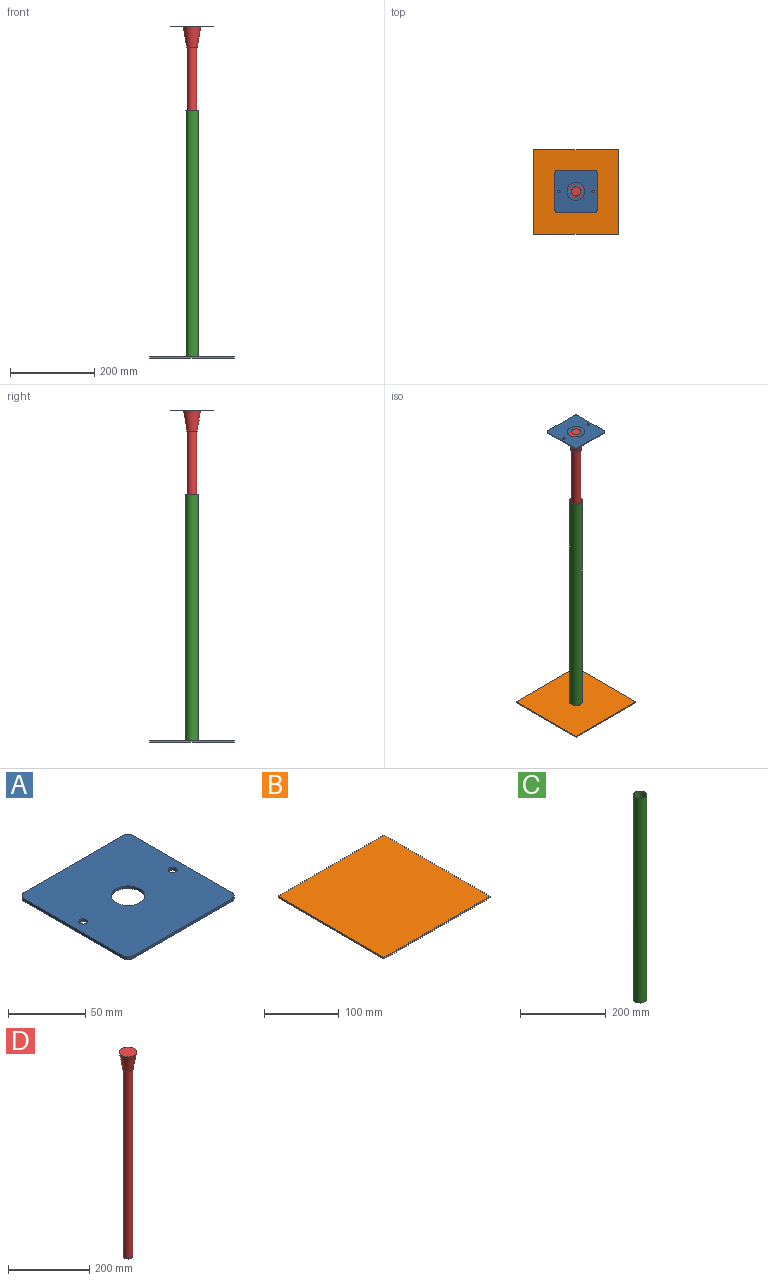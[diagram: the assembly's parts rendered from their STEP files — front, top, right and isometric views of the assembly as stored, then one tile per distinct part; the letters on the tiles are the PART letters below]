
ASSEMBLY  parts=4 mates=3
PART A: 13 faces, bbox 99.9x99.9x2.1 mm
  f0: plane 89.79x2.13mm, normal (0,-1,0), area 191.6mm2, adj f1,f7,f8,f9
  f1: cylinder r=5.08mm len=5.08mm, axis (0,0,-1), area 17mm2, adj f0,f2,f8,f9
  f2: plane 89.79x2.13mm, normal (1,0,0), area 191.6mm2, adj f1,f3,f8,f9
  f3: cylinder r=5.08mm len=5.08mm, axis (0,0,-1), area 17mm2, adj f2,f4,f8,f9
  f4: plane 89.79x2.13mm, normal (0,1,0), area 191.6mm2, adj f3,f5,f8,f9
  f5: cylinder r=5.08mm len=5.08mm, axis (0,0,-1), area 17mm2, adj f4,f6,f8,f9
  f6: plane 89.79x2.13mm, normal (-1,0,0), area 191.6mm2, adj f5,f7,f8,f9
  f7: cylinder r=5.08mm len=5.08mm, axis (0,0,-1), area 17mm2, adj f0,f6,f8,f9
  f8: plane 99.95x99.95mm, normal (0,0,1), area 9539.3mm2, adj f0,f1,f2,f3,f4,f5,f6,f7
  f9: plane 99.95x99.95mm, normal (0,0,-1), area 9539.3mm2, adj f0,f1,f2,f3,f4,f5,f6,f7
  f10: cylinder r=2.92mm len=5.84mm, axis (0,0,1), area 39.2mm2, adj f8,f9
  f11: cylinder r=2.92mm len=5.84mm, axis (0,0,1), area 39.2mm2, adj f8,f9
  f12: cylinder r=10.92mm len=21.84mm, axis (0,0,1), area 146.4mm2, adj f8,f9
PART B: 6 faces, bbox 200x200x2.5 mm
  f0: plane 200.03x2.54mm, normal (1,0,0), area 508.1mm2, adj f1,f3,f4,f5
  f1: plane 200.03x2.54mm, normal (0,1,0), area 508.1mm2, adj f0,f2,f4,f5
  f2: plane 200.03x2.54mm, normal (-1,0,0), area 508.1mm2, adj f1,f3,f4,f5
  f3: plane 200.03x2.54mm, normal (0,-1,0), area 508.1mm2, adj f0,f2,f4,f5
  f4: plane 200.03x200.03mm, normal (0,0,-1), area 40010mm2, adj f0,f1,f2,f3
  f5: plane 200.03x200.03mm, normal (0,0,1), area 40010mm2, adj f0,f1,f2,f3
PART C: 4 faces, bbox 30.5x30.5x584.2 mm
  f0: cylinder r=15.24mm len=584.2mm, axis (0,0,1), area 55940.5mm2, adj f1,f2
  f1: plane 30.48x30.48mm, normal (0,0,-1), area 109.2mm2, adj f0,f3
  f2: plane 30.48x30.48mm, normal (0,0,1), area 109.2mm2, adj f0,f3
  f3: cylinder r=14.05mm len=584.2mm, axis (0,0,1), area 51584.3mm2, adj f1,f2
PART D: 5 faces, bbox 42.7x42.7x616 mm
  f0: plane 42.67x42.67mm, normal (0,0,1), area 1430.1mm2, adj f2
  f1: plane 25.4x25.4mm, normal (0,0,-1), area 96.3mm2, adj f2,f3
  f2: cone r=21.34mm half-angle=9.6deg, axis (0,0,1), area 5509.8mm2, adj f0,f1
  f3: cylinder r=11.43mm len=565.15mm, axis (0,0,1), area 40587.3mm2, adj f1,f4
  f4: plane 22.86x22.86mm, normal (0,0,-1), area 410.4mm2, adj f3
PLACE A t=(420.91,-208.92,97.68)mm
PLACE B t=(420.91,-208.92,-88.77)mm
PLACE C t=(420.91,-208.92,-88.77)mm
PLACE D t=(420.91,-208.92,112.51)mm
MATE fastened A.f12 <-> D.f2  axis (0,0,1) through (420.91,-208.92,112.51)mm
MATE fastened C.f0 <-> B.f5  axis (0,0,1) through (420.91,-208.92,-672.97)mm
MATE slider D.f3 <-> C.f0  axis (0,0,1) through (420.91,-208.92,61.71)mm
